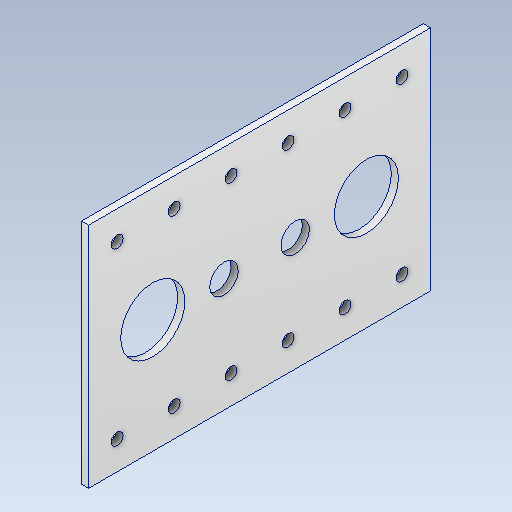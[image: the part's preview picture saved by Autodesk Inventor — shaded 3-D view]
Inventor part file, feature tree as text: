
AUTODESK INVENTOR PART (.ipt)
format: ipt  version: 2023 (Build 270158000, 158)  size: 146,432 bytes
history: native  units: in
note: dims shown in document units (in); Inventor stores cm internally (conversion verified against a paired STEP export)
features: extrude x1, sketch x1
ambient origin geometry x8: Origin, YZ Plane, XZ Plane, XY Plane, X Axis, Y Axis, Z Axis, Center Point
bodies: Solid1 (feature_tree)
feature tree (2):
  extrude  "Extrusion1"  Depth=6.0in
  sketch  "Sketch1"  dims[d0=4.0in d1=6.0in d2=1.125in d3=0.5in d4=0.5in d5=1.125in d6=1.25in d7=1.25in d8=1.25in d9=0.2087in d10=0.5in d11=0.5in d12=2.3622in d14=1.0in d15=0.7874in d17=3.0in d20=0.125in d21=0.0in d22=0.5in d23=0.0344in d24=0.5in d25=0.0344in]
